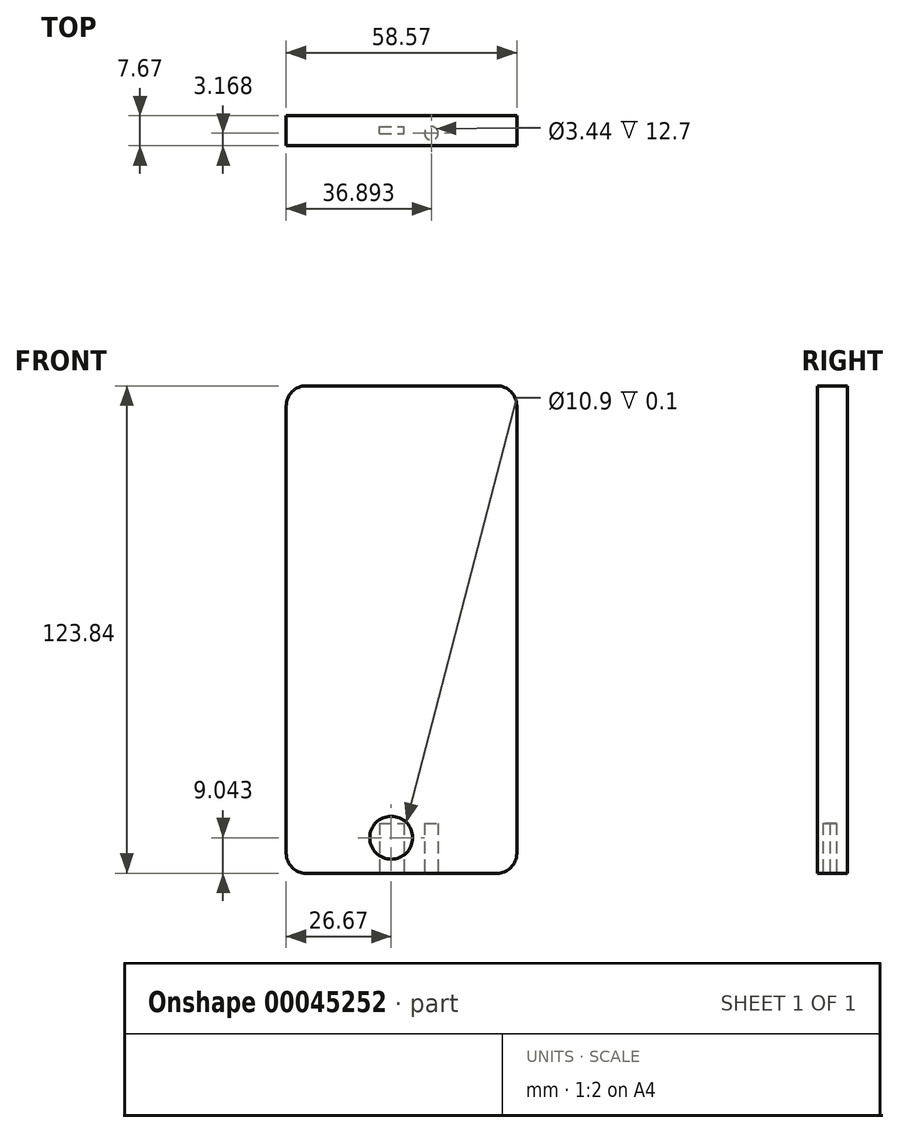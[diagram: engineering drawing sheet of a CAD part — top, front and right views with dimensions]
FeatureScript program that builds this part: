
annotation { "Feature Type Name" : "Feature", "Feature Type Description" : "" }
export const myFeature = defineFeature(function(context is Context, id is Id, definition is map)
    precondition{}
    {
        {
            var Q0;
            Q0=qCreatedBy(makeId("Front.planeOp"),FACE);
            var sketch = newSketch(context, id + "F0", { "sketchPlane" : qUnion([Q0])});
            skLineSegment(sketch, "E0", {"start": v(-26.96, 31.78) * mm, "end": v(-26.96, -92.06) * mm});
            skLineSegment(sketch, "E1", {"start": v(-26.96, -92.06) * mm, "end": v(31.6, -92.06) * mm});
            skLineSegment(sketch, "E2", {"start": v(31.6, -92.06) * mm, "end": v(31.6, 31.78) * mm});
            skLineSegment(sketch, "E3", {"start": v(31.6, 31.78) * mm, "end": v(-26.96, 31.78) * mm});
            skSolve(sketch);
        }
        {
            var Q0;
            Q0 = qSketchRegion(id + "F0", true);
            extrude(context, id + "F1", {"entities" : qUnion([Q0]), "depth" : 7.67 * mm});
        }
        {
            var Q0;
            Q0=makeQuery(id+"F1.opExtrude","SWEPT_EDGE",EDGE,{"disambiguationData":[OSD([sQuery(id+"F0.wireOp",EDGE,"E0"),sQuery(id+"F0.wireOp",EDGE,"E3")])]});
            fillet(context, id + "F2", {"entities" : qUnion([Q0]), "radius" : 5.08 * mm, "tangentPropagation" : true, "allowEdgeOverflow" : false});
        }
        {
            var Q0;
            Q0=makeQuery(id+"F1.opExtrude","SWEPT_EDGE",EDGE,{"disambiguationData":[OSD([sQuery(id+"F0.wireOp",EDGE,"E2"),sQuery(id+"F0.wireOp",EDGE,"E3")])]});
            fillet(context, id + "F3", {"entities" : qUnion([Q0]), "radius" : 5.08 * mm, "tangentPropagation" : true, "allowEdgeOverflow" : false});
        }
        {
            var Q0;
            Q0=makeQuery(id+"F1.opExtrude","SWEPT_EDGE",EDGE,{"disambiguationData":[OSD([sQuery(id+"F0.wireOp",EDGE,"E1"),sQuery(id+"F0.wireOp",EDGE,"E2")])]});
            fillet(context, id + "F4", {"entities" : qUnion([Q0]), "radius" : 5.08 * mm, "tangentPropagation" : true, "allowEdgeOverflow" : false});
        }
        {
            var Q0;
            Q0=makeQuery(id+"F1.opExtrude","SWEPT_EDGE",EDGE,{"disambiguationData":[OSD([sQuery(id+"F0.wireOp",EDGE,"E0"),sQuery(id+"F0.wireOp",EDGE,"E1")])]});
            fillet(context, id + "F5", {"entities" : qUnion([Q0]), "radius" : 5.08 * mm, "tangentPropagation" : true, "allowEdgeOverflow" : false});
        }
        {
            var Q0;
            Q0=makeQuery(id+"F1.opExtrude","CAP_FACE",FACE,{"disambiguationData":[OSD([sQuery(id+"F0.wireOp",EDGE,"E0"),sQuery(id+"F0.wireOp",EDGE,"E1"),sQuery(id+"F0.wireOp",EDGE,"E2"),sQuery(id+"F0.wireOp",EDGE,"E3")])],"isStart":false});
            var sketch = newSketch(context, id + "F6", { "sketchPlane" : qUnion([Q0])});
            skLineSegment(sketch, "E4", {"start": v(-23.53, 15.05) * mm, "end": v(-23.53, -75.34) * mm});
            skLineSegment(sketch, "E5", {"start": v(-23.53, -75.34) * mm, "end": v(28.17, -75.34) * mm});
            skLineSegment(sketch, "E6", {"start": v(28.17, -75.34) * mm, "end": v(28.17, 15.05) * mm});
            skLineSegment(sketch, "E7", {"start": v(28.17, 15.05) * mm, "end": v(-23.53, 15.05) * mm});
            skLineSegment(sketch, "E8", {"start": v(2.32, 15.05) * mm, "end": v(2.32, 31.78) * mm, "construction": true});
            skSolve(sketch);
        }
        {
            var Q0;
            Q0=makeQuery(id+"F6.imprint","IMPRINT",FACE,{"disambiguationData":[TD([[makeQuery(id+"F6.imprint","IMPRINT",EDGE,{"derivedFrom":sQuery(id+"F6.wireOp",EDGE,"E4")}),-1.0]])]});
            var sketch = newSketch(context, id + "F7", { "sketchPlane" : qUnion([Q0])});
            skCircle(sketch, "E9", {"center": v(-0.29, -83.02) * mm, "radius": 5.45 * mm});
            skSolve(sketch);
        }
        {
            var Q0;
            Q0=makeQuery(id+"F1.opExtrude","SWEPT_FACE",FACE,{"disambiguationData":[OSD([sQuery(id+"F0.wireOp",EDGE,"E1")])]});
            var sketch = newSketch(context, id + "F8", { "sketchPlane" : qUnion([Q0])});
            skLineSegment(sketch, "E10.bottom", {"start": v(-3.25, 4.52) * mm, "end": v(2.97, 4.52) * mm});
            skLineSegment(sketch, "E10.top", {"start": v(-3.25, 2.78) * mm, "end": v(2.97, 2.78) * mm});
            skLineSegment(sketch, "E10.left", {"start": v(-3.25, 4.52) * mm, "end": v(-3.25, 2.78) * mm});
            skLineSegment(sketch, "E10.right", {"start": v(2.97, 4.52) * mm, "end": v(2.97, 2.78) * mm});
            skSolve(sketch);
        }
        {
            var Q0;
            Q0 = qSketchRegion(id + "F8", true);
            extrude(context, id + "F9", {"entities" : qUnion([Q0]), "operationType" : NewBodyOperationType.REMOVE, "oppositeDirection" : true, "depth" : 12.7 * mm});
        }
        {
            var Q0;
            Q0=makeQuery(id+"F1.opExtrude","SWEPT_FACE",FACE,{"disambiguationData":[OSD([sQuery(id+"F0.wireOp",EDGE,"E1")])]});
            var sketch = newSketch(context, id + "F10", { "sketchPlane" : qUnion([Q0])});
            skCircle(sketch, "E11", {"center": v(9.93, 4.5) * mm, "radius": 1.72 * mm});
            skSolve(sketch);
        }
        {
            var Q0;
            Q0 = qSketchRegion(id + "F10", true);
            extrude(context, id + "F11", {"entities" : qUnion([Q0]), "operationType" : NewBodyOperationType.REMOVE, "oppositeDirection" : true, "depth" : 12.7 * mm});
        }
        {
            var Q0;
            Q0=makeQuery(id+"F7.imprint","IMPRINT",FACE,{"disambiguationData":[TD([[makeQuery(id+"F7.imprint","IMPRINT",EDGE,{"derivedFrom":sQuery(id+"F7.wireOp",EDGE,"E9")}),1.0]])]});
            extrude(context, id + "F12", {"entities" : qUnion([Q0]), "operationType" : NewBodyOperationType.REMOVE, "oppositeDirection" : true, "depth" : .10 * mm});
        }
    });
